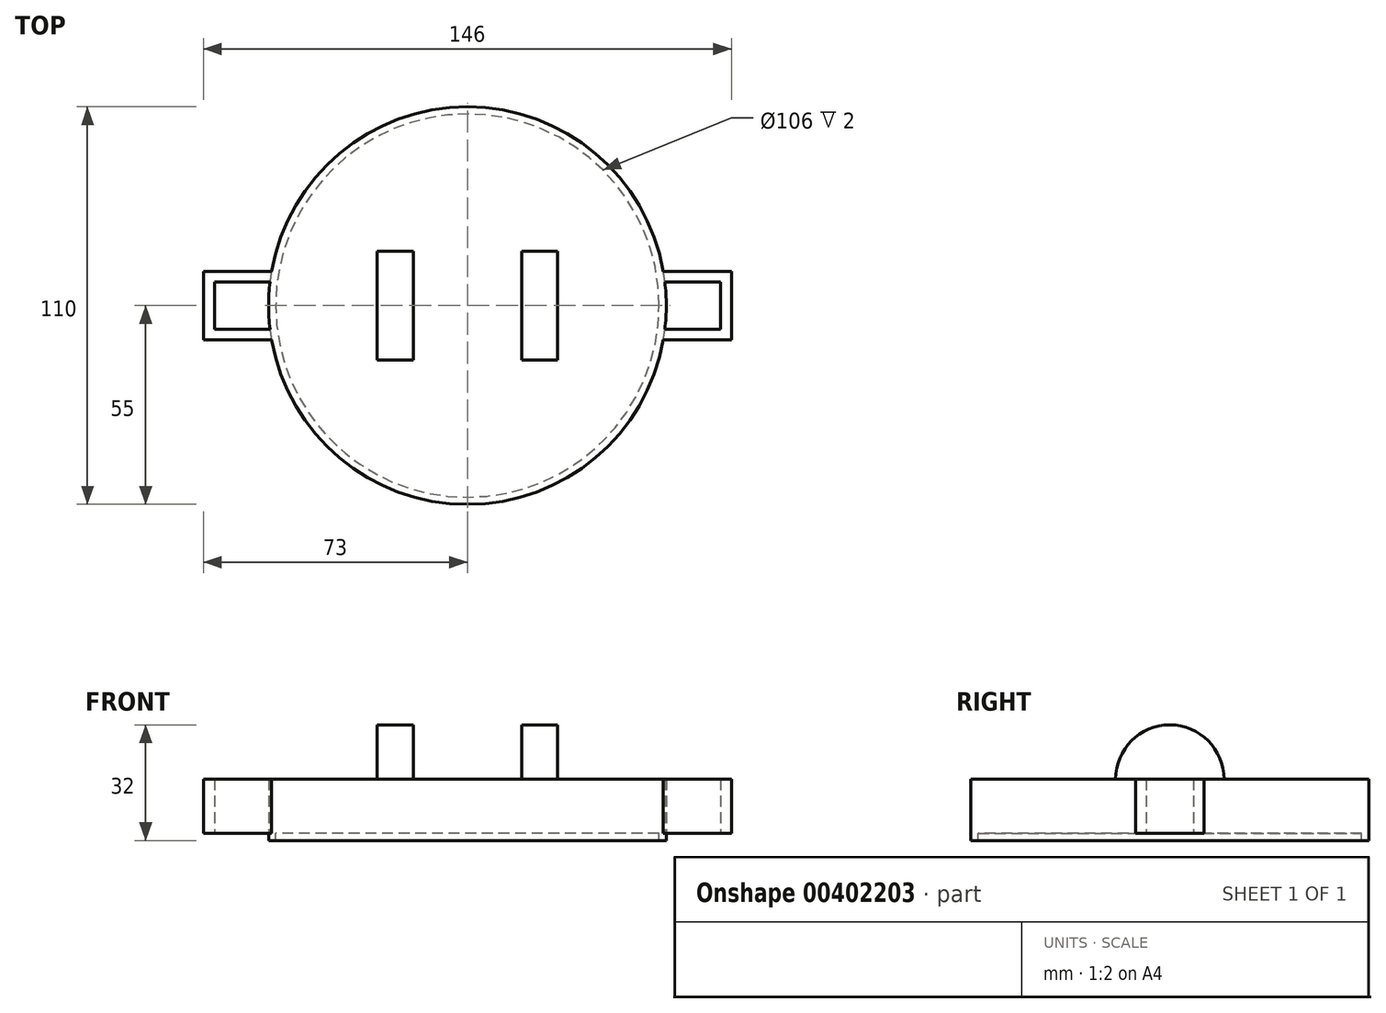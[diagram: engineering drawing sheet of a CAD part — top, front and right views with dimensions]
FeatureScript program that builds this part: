
annotation { "Feature Type Name" : "Feature", "Feature Type Description" : "" }
export const myFeature = defineFeature(function(context is Context, id is Id, definition is map)
    precondition{}
    {
        {
            var Q0;
            Q0=qCreatedBy(makeId("Top.planeOp"),FACE);
            var sketch = newSketch(context, id + "F0", { "sketchPlane" : qUnion([Q0])});
            skCircle(sketch, "E0", {"center": v(0, 0) * mm, "radius": 55 * mm});
            skCircle(sketch, "E1", {"center": v(0, 0) * mm, "radius": 53 * mm});
            skSolve(sketch);
        }
        {
            var Q0;
            Q0=makeQuery(id+"F0.imprint","IMPRINT",FACE,{"disambiguationData":[TD([[makeQuery(id+"F0.imprint","IMPRINT",EDGE,{"derivedFrom":sQuery(id+"F0.wireOp",EDGE,"E0")}),1.0]])]});
            var Q1;
            Q1=makeQuery(id+"F0.imprint","IMPRINT",FACE,{"disambiguationData":[TD([[makeQuery(id+"F0.imprint","IMPRINT",EDGE,{"derivedFrom":sQuery(id+"F0.wireOp",EDGE,"E1")}),1.0]])]});
            extrude(context, id + "F1", {"entities" : qUnion([Q0, Q1]), "depth" : 15 * mm});
        }
        {
            var Q0;
            Q0=qCreatedBy(makeId("Top.planeOp"),FACE);
            var sketch = newSketch(context, id + "F2", { "sketchPlane" : qUnion([Q0])});
            skCircle(sketch, "E2", {"center": v(0, 0) * mm, "radius": 53 * mm});
            skCircle(sketch, "E3", {"center": v(0, 0) * mm, "radius": 55 * mm});
            skSolve(sketch);
        }
        {
            var Q0;
            Q0=makeQuery(id+"F2.imprint","IMPRINT",FACE,{"disambiguationData":[TD([[makeQuery(id+"F2.imprint","IMPRINT",EDGE,{"derivedFrom":sQuery(id+"F2.wireOp",EDGE,"E2")}),-1.0]])]});
            extrude(context, id + "F3", {"entities" : qUnion([Q0]), "operationType" : NewBodyOperationType.ADD, "oppositeDirection" : true, "depth" : 2 * mm});
        }
        {
            var Q0;
            Q0=makeQuery(id+"F1.opExtrude","CAP_FACE",FACE,{"disambiguationData":[OSD([sQuery(id+"F0.wireOp",EDGE,"E0")])],"isStart":false});
            var sketch = newSketch(context, id + "F4", { "sketchPlane" : qUnion([Q0])});
            skLineSegment(sketch, "E4", {"start": v(-25, 15) * mm, "end": v(-15, 15) * mm});
            skLineSegment(sketch, "E5.MirrorCS", {"start": v(-25, -15) * mm, "end": v(-15, -15) * mm});
            skLineSegment(sketch, "E6", {"start": v(-25, 15) * mm, "end": v(-25, -15) * mm});
            skLineSegment(sketch, "E7", {"start": v(-15, 15) * mm, "end": v(-15, -15) * mm});
            skLineSegment(sketch, "E8.MirrorCS", {"start": v(25, 15) * mm, "end": v(15, 15) * mm});
            skLineSegment(sketch, "E9.MirrorCS", {"start": v(25, 15) * mm, "end": v(25, -15) * mm});
            skLineSegment(sketch, "E10.MirrorCS", {"start": v(15, 15) * mm, "end": v(15, -15) * mm});
            skLineSegment(sketch, "E11.MirrorCS", {"start": v(25, -15) * mm, "end": v(15, -15) * mm});
            skLineSegment(sketch, "E12", {"start": v(-25, 0) * mm, "end": v(-15, 0) * mm});
            skLineSegment(sketch, "E13", {"start": v(15, 0) * mm, "end": v(25, 0) * mm});
            skLineSegment(sketch, "E14", {"start": v(-75.92, 0) * mm, "end": v(82.56, 0) * mm});
            skPoint(sketch, "E14.startSnap0", {"position": v(-20, 0) * mm});
            skSolve(sketch);
        }
        {
            var Q0;
            {var subQ0=sQuery(id+"F4.wireOp",EDGE,"E4");Q0=makeQuery(id+"F4.imprint","IMPRINT",FACE,{"disambiguationData":[TD([[makeQuery(id+"F4.imprint","IMPRINT",EDGE,{"derivedFrom":subQ0}),-1.0]])]});}
            var Q1;
            {var subQ0=sQuery(id+"F4.wireOp",EDGE,"E8.MirrorCS");Q1=makeQuery(id+"F4.imprint","IMPRINT",FACE,{"disambiguationData":[TD([[makeQuery(id+"F4.imprint","IMPRINT",EDGE,{"derivedFrom":subQ0}),1.0]])]});}
            var Q2;
            Q2=sQuery(id+"F4.wireOp",EDGE,"E14");
            revolve(context, id + "F5", {"operationType" : NewBodyOperationType.ADD, "entities" : qUnion([Q0, Q1]), "axis" : qUnion([Q2]), "revolveType" : RevolveType.ONE_DIRECTION, "angle" : 180 * degree});
        }
        {
            var Q0;
            Q0=qCreatedBy(makeId("Top.planeOp"),FACE);
            var sketch = newSketch(context, id + "F6", { "sketchPlane" : qUnion([Q0])});
            skLineSegment(sketch, "E15", {"start": v(-53.27, 6.5) * mm, "end": v(-70, 6.5) * mm});
            skLineSegment(sketch, "E16", {"start": v(-70, 6.5) * mm, "end": v(-70, 0) * mm});
            skLineSegment(sketch, "E17.MirrorCS", {"start": v(-53.27, -6.5) * mm, "end": v(-70, -6.5) * mm});
            skLineSegment(sketch, "E18.MirrorCS", {"start": v(-70, -6.5) * mm, "end": v(-70, 0) * mm});
            skLineSegment(sketch, "E19.0", {"start": v(-52.23, -9.5) * mm, "end": v(-73, -9.5) * mm});
            skLineSegment(sketch, "E19.1", {"start": v(-73, -9.5) * mm, "end": v(-73, 0) * mm});
            skLineSegment(sketch, "E19.2", {"start": v(-73, 9.5) * mm, "end": v(-73, 0) * mm});
            skLineSegment(sketch, "E19.3", {"start": v(-52.23, 9.5) * mm, "end": v(-73, 9.5) * mm});
            skLineSegment(sketch, "E20.MirrorCS", {"start": v(52.23, 9.5) * mm, "end": v(73, 9.5) * mm});
            skLineSegment(sketch, "E21.MirrorCS", {"start": v(73, 9.5) * mm, "end": v(73, 0) * mm});
            skLineSegment(sketch, "E22.MirrorCS", {"start": v(73, -9.5) * mm, "end": v(73, 0) * mm});
            skLineSegment(sketch, "E23.MirrorCS", {"start": v(52.23, -9.5) * mm, "end": v(73, -9.5) * mm});
            skLineSegment(sketch, "E24.MirrorCS", {"start": v(53.27, -6.5) * mm, "end": v(70, -6.5) * mm});
            skLineSegment(sketch, "E25.MirrorCS", {"start": v(70, -6.5) * mm, "end": v(70, 0) * mm});
            skLineSegment(sketch, "E26.MirrorCS", {"start": v(70, 6.5) * mm, "end": v(70, 0) * mm});
            skLineSegment(sketch, "E27.MirrorCS", {"start": v(53.27, 6.5) * mm, "end": v(70, 6.5) * mm});
            skLineSegment(sketch, "E28", {"start": v(-53.27, 6.5) * mm, "end": v(-52.23, 9.5) * mm});
            skLineSegment(sketch, "E29", {"start": v(-52.23, -9.5) * mm, "end": v(-53.27, -6.5) * mm});
            skLineSegment(sketch, "E30.MirrorCS", {"start": v(53.27, 6.5) * mm, "end": v(52.23, 9.5) * mm});
            skLineSegment(sketch, "E31.MirrorCS", {"start": v(52.23, -9.5) * mm, "end": v(53.27, -6.5) * mm});
            skSolve(sketch);
        }
        {
            var Q0;
            Q0 = qSketchRegion(id + "F6", true);
            extrude(context, id + "F7", {"entities" : qUnion([Q0]), "operationType" : NewBodyOperationType.ADD, "depth" : 15 * mm});
        }
    });
